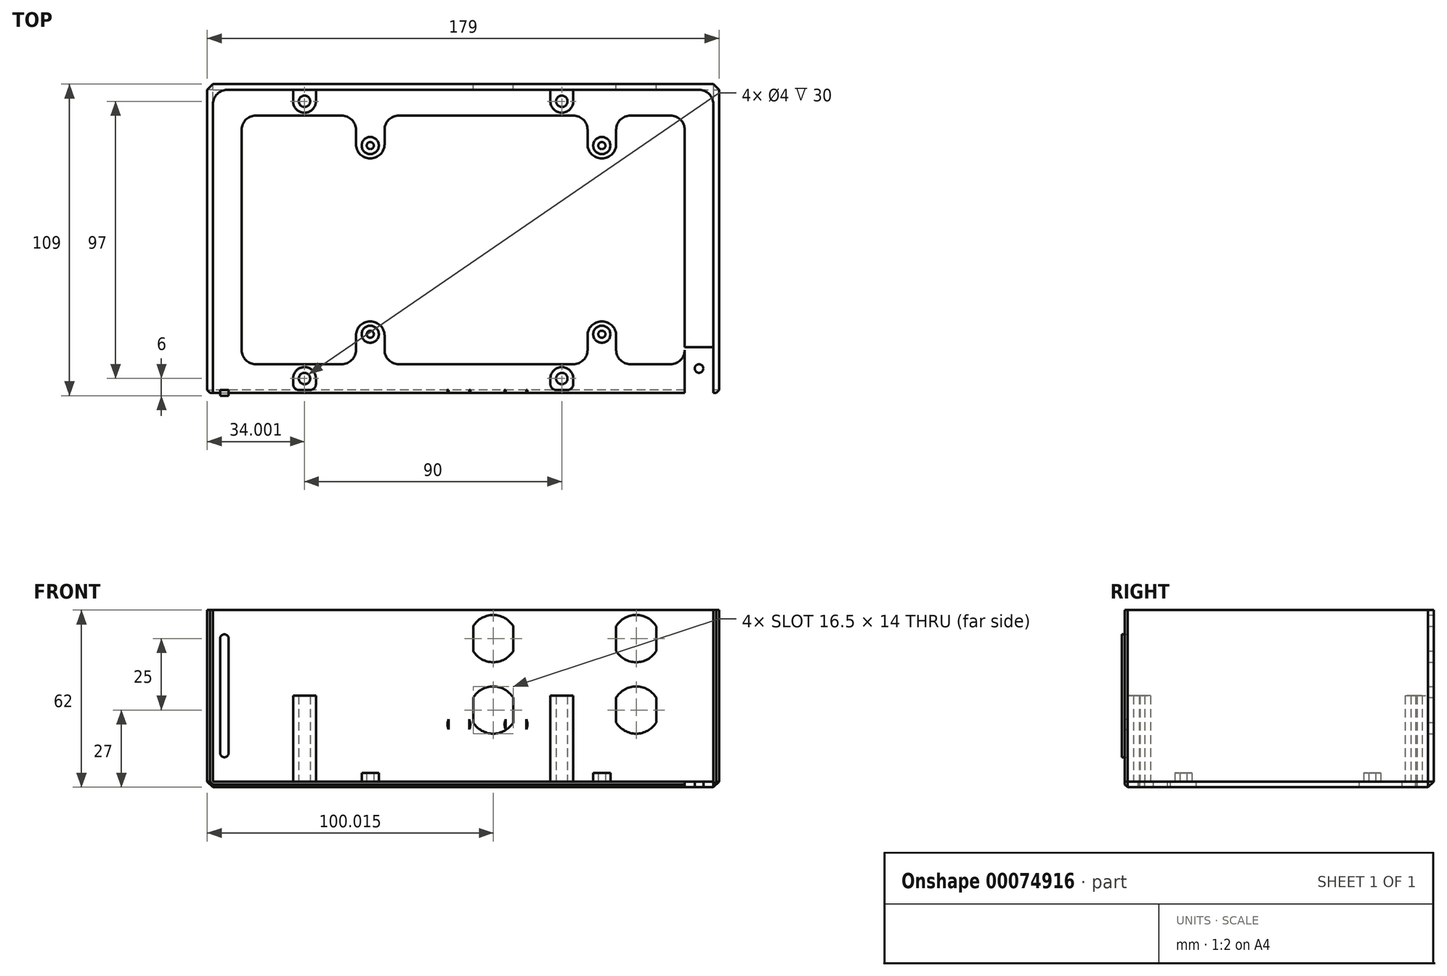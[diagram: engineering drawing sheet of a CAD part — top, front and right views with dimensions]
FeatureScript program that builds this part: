
annotation { "Feature Type Name" : "Feature", "Feature Type Description" : "" }
export const myFeature = defineFeature(function(context is Context, id is Id, definition is map)
    precondition{}
    {
        {
            var Q0;
            Q0=qCreatedBy(makeId("Top.planeOp"),FACE);
            var sketch = newSketch(context, id + "F0", { "sketchPlane" : qUnion([Q0])});
            skLineSegment(sketch, "E0.bottom", {"start": v(-80.27, 52.5) * mm, "end": v(94.73, 52.5) * mm});
            skLineSegment(sketch, "E0.top", {"start": v(-80.27, -52.5) * mm, "end": v(94.73, -52.5) * mm});
            skLineSegment(sketch, "E0.left", {"start": v(-80.27, 52.5) * mm, "end": v(-80.27, -52.5) * mm});
            skLineSegment(sketch, "E0.right", {"start": v(94.73, 52.5) * mm, "end": v(94.73, -52.5) * mm});
            skCircle(sketch, "E1", {"center": v(-25.27, 33) * mm, "radius": 1.25 * mm});
            skCircle(sketch, "E2.0.1.0", {"center": v(-25.27, -33) * mm, "radius": 1.25 * mm});
            skCircle(sketch, "E2.1.0.0", {"center": v(55.73, 33) * mm, "radius": 1.25 * mm});
            skCircle(sketch, "E2.1.1.0", {"center": v(55.73, -33) * mm, "radius": 1.25 * mm});
            skLineSegment(sketch, "E2.direction1", {"start": v(-25.27, 33) * mm, "end": v(55.73, 33) * mm, "construction": true});
            skLineSegment(sketch, "E2.direction2", {"start": v(-25.27, 33) * mm, "end": v(-25.27, -33) * mm, "construction": true});
            skLineSegment(sketch, "E3.bottom", {"start": v(-82.27, 54.5) * mm, "end": v(96.73, 54.5) * mm});
            skLineSegment(sketch, "E3.top", {"start": v(-82.27, -54.5) * mm, "end": v(96.73, -54.5) * mm});
            skLineSegment(sketch, "E3.left", {"start": v(-82.27, 54.5) * mm, "end": v(-82.27, -54.5) * mm});
            skLineSegment(sketch, "E3.right", {"start": v(96.73, 54.5) * mm, "end": v(96.73, -54.5) * mm});
            skCircle(sketch, "E4", {"center": v(-25.27, 33) * mm, "radius": 3 * mm});
            skCircle(sketch, "E5.0.1.0", {"center": v(-25.27, -33) * mm, "radius": 3 * mm});
            skCircle(sketch, "E5.1.0.0", {"center": v(55.73, 33) * mm, "radius": 3 * mm});
            skCircle(sketch, "E5.1.1.0", {"center": v(55.73, -33) * mm, "radius": 3 * mm});
            skLineSegment(sketch, "E6.bottom", {"start": v(-48.27, 42.5) * mm, "end": v(75.73, 42.5) * mm});
            skLineSegment(sketch, "E6.top", {"start": v(-48.27, -42.5) * mm, "end": v(75.73, -42.5) * mm});
            skLineSegment(sketch, "E6.left", {"start": v(-48.27, 42.5) * mm, "end": v(-48.27, -42.5) * mm});
            skLineSegment(sketch, "E6.right", {"start": v(75.73, 42.5) * mm, "end": v(75.73, -42.5) * mm});
            skCircle(sketch, "E7", {"center": v(-48.27, -48.5) * mm, "radius": 2 * mm});
            skCircle(sketch, "E8", {"center": v(-48.27, -48.5) * mm, "radius": 4 * mm});
            skCircle(sketch, "E9.0.1.0", {"center": v(-48.27, 48.5) * mm, "radius": 4 * mm});
            skCircle(sketch, "E9.0.1.1", {"center": v(-48.27, 48.5) * mm, "radius": 2 * mm});
            skCircle(sketch, "E9.1.0.0", {"center": v(41.73, -48.5) * mm, "radius": 4 * mm});
            skCircle(sketch, "E9.1.0.1", {"center": v(41.73, -48.5) * mm, "radius": 2 * mm});
            skCircle(sketch, "E9.1.1.0", {"center": v(41.73, 48.5) * mm, "radius": 4 * mm});
            skCircle(sketch, "E9.1.1.1", {"center": v(41.73, 48.5) * mm, "radius": 2 * mm});
            skLineSegment(sketch, "E9.direction1", {"start": v(-48.27, -48.5) * mm, "end": v(41.73, -48.5) * mm, "construction": true});
            skLineSegment(sketch, "E9.direction2", {"start": v(-48.27, -48.5) * mm, "end": v(-48.27, 48.5) * mm, "construction": true});
            skLineSegment(sketch, "E10", {"start": v(-52.27, -48.55) * mm, "end": v(-52.22, -52.5) * mm});
            skLineSegment(sketch, "E11", {"start": v(-44.27, -48.5) * mm, "end": v(-44.27, -52.5) * mm});
            skLineSegment(sketch, "E12", {"start": v(-52.26, 48.76) * mm, "end": v(-52.26, 52.5) * mm});
            skLineSegment(sketch, "E13", {"start": v(-44.27, 48.54) * mm, "end": v(-44.27, 52.5) * mm});
            skLineSegment(sketch, "E14", {"start": v(37.74, 48.16) * mm, "end": v(37.74, 52.5) * mm});
            skLineSegment(sketch, "E15", {"start": v(45.73, 48.44) * mm, "end": v(45.73, 52.5) * mm});
            skLineSegment(sketch, "E16.MirrorCS", {"start": v(37.74, -48.16) * mm, "end": v(37.74, -52.5) * mm});
            skLineSegment(sketch, "E17.MirrorCS", {"start": v(45.73, -48.44) * mm, "end": v(45.73, -52.5) * mm});
            skLineSegment(sketch, "E18.bottom", {"start": v(94.73, 27.5) * mm, "end": v(84.73, 27.5) * mm});
            skLineSegment(sketch, "E18.top", {"start": v(94.73, 12.5) * mm, "end": v(84.73, 12.5) * mm});
            skLineSegment(sketch, "E18.left", {"start": v(94.73, 27.5) * mm, "end": v(94.73, 12.5) * mm});
            skLineSegment(sketch, "E18.right", {"start": v(84.73, 27.5) * mm, "end": v(84.73, 12.5) * mm});
            skCircle(sketch, "E19", {"center": v(89.73, 20) * mm, "radius": 1.5 * mm});
            skPoint(sketch, "E19.centerSnap0", {"position": v(89.73, 12.5) * mm});
            skPoint(sketch, "E19.centerSnap1", {"position": v(94.73, 20) * mm});
            skLineSegment(sketch, "E20.bottom", {"start": v(94.73, -52.5) * mm, "end": v(84.73, -52.5) * mm});
            skLineSegment(sketch, "E20.top", {"start": v(94.73, -37.5) * mm, "end": v(84.73, -37.5) * mm});
            skLineSegment(sketch, "E20.left", {"start": v(94.73, -52.5) * mm, "end": v(94.73, -37.5) * mm});
            skLineSegment(sketch, "E20.right", {"start": v(84.73, -52.5) * mm, "end": v(84.73, -37.5) * mm});
            skCircle(sketch, "E21", {"center": v(89.73, -45) * mm, "radius": 1.5 * mm});
            skPoint(sketch, "E21.centerSnap0", {"position": v(94.73, -45) * mm});
            skPoint(sketch, "E21.centerSnap1", {"position": v(89.73, -52.5) * mm});
            skSolve(sketch);
        }
        {
            var Q0;
            Q0=qSketchRegion(id+"F0",true);
            var Q1;
            Q1=makeQuery(id+"F0.imprint","IMPRINT",FACE,{"disambiguationData":[TD([[makeQuery(id+"F0.imprint","IMPRINT",EDGE,{"derivedFrom":sQuery(id+"F0.wireOp",EDGE,"E0.bottom")}),-1.0]])]});
            var Q2;
            Q2=makeQuery(id+"F0.imprint","IMPRINT",FACE,{"disambiguationData":[TD([[makeQuery(id+"F0.imprint","IMPRINT",EDGE,{"derivedFrom":sQuery(id+"F0.wireOp",EDGE,"E2.1.1.0")}),-1.0]])]});
            var Q3;
            Q3=makeQuery(id+"F0.imprint","IMPRINT",FACE,{"disambiguationData":[TD([[makeQuery(id+"F0.imprint","IMPRINT",EDGE,{"derivedFrom":sQuery(id+"F0.wireOp",EDGE,"E2.1.1.0")}),1.0]])]});
            var Q4;
            Q4=makeQuery(id+"F0.imprint","IMPRINT",FACE,{"disambiguationData":[TD([[makeQuery(id+"F0.imprint","IMPRINT",EDGE,{"derivedFrom":sQuery(id+"F0.wireOp",EDGE,"E2.0.1.0")}),-1.0]])]});
            var Q5;
            Q5=makeQuery(id+"F0.imprint","IMPRINT",FACE,{"disambiguationData":[TD([[makeQuery(id+"F0.imprint","IMPRINT",EDGE,{"derivedFrom":sQuery(id+"F0.wireOp",EDGE,"E2.0.1.0")}),1.0]])]});
            var Q6;
            Q6=makeQuery(id+"F0.imprint","IMPRINT",FACE,{"disambiguationData":[TD([[makeQuery(id+"F0.imprint","IMPRINT",EDGE,{"derivedFrom":sQuery(id+"F0.wireOp",EDGE,"E1")}),-1.0]])]});
            var Q7;
            Q7=makeQuery(id+"F0.imprint","IMPRINT",FACE,{"disambiguationData":[TD([[makeQuery(id+"F0.imprint","IMPRINT",EDGE,{"derivedFrom":sQuery(id+"F0.wireOp",EDGE,"E1")}),1.0]])]});
            var Q8;
            Q8=makeQuery(id+"F0.imprint","IMPRINT",FACE,{"disambiguationData":[TD([[makeQuery(id+"F0.imprint","IMPRINT",EDGE,{"derivedFrom":sQuery(id+"F0.wireOp",EDGE,"E2.1.0.0")}),-1.0]])]});
            var Q9;
            Q9=makeQuery(id+"F0.imprint","IMPRINT",FACE,{"disambiguationData":[TD([[makeQuery(id+"F0.imprint","IMPRINT",EDGE,{"derivedFrom":sQuery(id+"F0.wireOp",EDGE,"E2.1.0.0")}),1.0]])]});
            var Q10;
            Q10=makeQuery(id+"F0.imprint","IMPRINT",FACE,{"disambiguationData":[TD([[makeQuery(id+"F0.imprint","IMPRINT",EDGE,{"derivedFrom":sQuery(id+"F0.wireOp",EDGE,"E4")}),-1.0]])]});
            var Q11;
            Q11=makeQuery(id+"F0.imprint","IMPRINT",FACE,{"disambiguationData":[TD([[makeQuery(id+"F0.imprint","IMPRINT",EDGE,{"derivedFrom":sQuery(id+"F0.wireOp",EDGE,"E9.1.0.1")}),-1.0]])]});
            var Q12;
            Q12=makeQuery(id+"F0.imprint","IMPRINT",FACE,{"disambiguationData":[TD([[makeQuery(id+"F0.imprint","IMPRINT",EDGE,{"derivedFrom":sQuery(id+"F0.wireOp",EDGE,"E9.1.0.1")}),1.0]])]});
            var Q13;
            {var subQ0=sQuery(id+"F0.wireOp",EDGE,"E16.MirrorCS");var subQ1=sQuery(id+"F0.wireOp",EDGE,"E0.top");var subQ2=makeQuery(id+"F0.imprint","INTERSECT",VERTEX,{"derivedFrom":[subQ1,subQ0]});Q13=makeQuery(id+"F0.imprint","IMPRINT",FACE,{"disambiguationData":[TD([[makeQuery(id+"F0.imprint","IMPRINT",EDGE,{"disambiguationData":[TD([[subQ2,-1.0]])],"derivedFrom":subQ1}),1.0]])]});}
            var Q14;
            Q14=makeQuery(id+"F0.imprint","IMPRINT",FACE,{"disambiguationData":[TD([[makeQuery(id+"F0.imprint","IMPRINT",EDGE,{"derivedFrom":sQuery(id+"F0.wireOp",EDGE,"E7")}),-1.0]])]});
            var Q15;
            Q15=makeQuery(id+"F0.imprint","IMPRINT",FACE,{"disambiguationData":[TD([[makeQuery(id+"F0.imprint","IMPRINT",EDGE,{"derivedFrom":sQuery(id+"F0.wireOp",EDGE,"E7")}),1.0]])]});
            var Q16;
            {var subQ0=sQuery(id+"F0.wireOp",EDGE,"E10");Q16=makeQuery(id+"F0.imprint","IMPRINT",FACE,{"disambiguationData":[TD([[makeQuery(id+"F0.imprint","IMPRINT",EDGE,{"derivedFrom":subQ0}),1.0]])]});}
            var Q17;
            {var subQ0=sQuery(id+"F0.wireOp",EDGE,"E11");Q17=makeQuery(id+"F0.imprint","IMPRINT",FACE,{"disambiguationData":[TD([[makeQuery(id+"F0.imprint","IMPRINT",EDGE,{"derivedFrom":subQ0}),-1.0]])]});}
            var Q18;
            Q18=makeQuery(id+"F0.imprint","IMPRINT",FACE,{"disambiguationData":[TD([[makeQuery(id+"F0.imprint","IMPRINT",EDGE,{"derivedFrom":sQuery(id+"F0.wireOp",EDGE,"E9.0.1.1")}),-1.0]])]});
            var Q19;
            Q19=makeQuery(id+"F0.imprint","IMPRINT",FACE,{"disambiguationData":[TD([[makeQuery(id+"F0.imprint","IMPRINT",EDGE,{"derivedFrom":sQuery(id+"F0.wireOp",EDGE,"E9.0.1.1")}),1.0]])]});
            var Q20;
            {var subQ0=sQuery(id+"F0.wireOp",EDGE,"E13");Q20=makeQuery(id+"F0.imprint","IMPRINT",FACE,{"disambiguationData":[TD([[makeQuery(id+"F0.imprint","IMPRINT",EDGE,{"derivedFrom":subQ0}),1.0]])]});}
            var Q21;
            {var subQ0=sQuery(id+"F0.wireOp",EDGE,"E12");Q21=makeQuery(id+"F0.imprint","IMPRINT",FACE,{"disambiguationData":[TD([[makeQuery(id+"F0.imprint","IMPRINT",EDGE,{"derivedFrom":subQ0}),-1.0]])]});}
            var Q22;
            {var subQ0=sQuery(id+"F0.wireOp",EDGE,"E17.MirrorCS");var subQ1=sQuery(id+"F0.wireOp",EDGE,"E0.top");var subQ2=makeQuery(id+"F0.imprint","INTERSECT",VERTEX,{"derivedFrom":[subQ1,subQ0]});Q22=makeQuery(id+"F0.imprint","IMPRINT",FACE,{"disambiguationData":[TD([[makeQuery(id+"F0.imprint","IMPRINT",EDGE,{"disambiguationData":[TD([[subQ2,1.0]])],"derivedFrom":subQ1}),1.0]])]});}
            var Q23;
            {var subQ0=sQuery(id+"F0.wireOp",EDGE,"E14");var subQ1=sQuery(id+"F0.wireOp",EDGE,"E0.bottom");var subQ2=makeQuery(id+"F0.imprint","INTERSECT",VERTEX,{"derivedFrom":[subQ1,subQ0]});Q23=makeQuery(id+"F0.imprint","IMPRINT",FACE,{"disambiguationData":[TD([[makeQuery(id+"F0.imprint","IMPRINT",EDGE,{"disambiguationData":[TD([[subQ2,-1.0]])],"derivedFrom":subQ1}),-1.0]])]});}
            var Q24;
            {var subQ0=sQuery(id+"F0.wireOp",EDGE,"E15");var subQ1=sQuery(id+"F0.wireOp",EDGE,"E0.bottom");var subQ2=makeQuery(id+"F0.imprint","INTERSECT",VERTEX,{"derivedFrom":[subQ1,subQ0]});Q24=makeQuery(id+"F0.imprint","IMPRINT",FACE,{"disambiguationData":[TD([[makeQuery(id+"F0.imprint","IMPRINT",EDGE,{"disambiguationData":[TD([[subQ2,1.0]])],"derivedFrom":subQ1}),-1.0]])]});}
            var Q25;
            Q25=makeQuery(id+"F0.imprint","IMPRINT",FACE,{"disambiguationData":[TD([[makeQuery(id+"F0.imprint","IMPRINT",EDGE,{"derivedFrom":sQuery(id+"F0.wireOp",EDGE,"E9.1.1.1")}),-1.0]])]});
            var Q26;
            Q26=makeQuery(id+"F0.imprint","IMPRINT",FACE,{"disambiguationData":[TD([[makeQuery(id+"F0.imprint","IMPRINT",EDGE,{"derivedFrom":sQuery(id+"F0.wireOp",EDGE,"E9.1.1.1")}),1.0]])]});
            var Q27;
            Q27=makeQuery(id+"F0.imprint","IMPRINT",FACE,{"disambiguationData":[TD([[makeQuery(id+"F0.imprint","IMPRINT",EDGE,{"derivedFrom":sQuery(id+"F0.wireOp",EDGE,"E18.bottom")}),1.0]])]});
            var Q28;
            Q28=makeQuery(id+"F0.imprint","IMPRINT",FACE,{"disambiguationData":[TD([[makeQuery(id+"F0.imprint","IMPRINT",EDGE,{"derivedFrom":sQuery(id+"F0.wireOp",EDGE,"E20.bottom")}),-1.0]])]});
            var Q29;
            Q29=makeQuery(id+"F0.imprint","IMPRINT",FACE,{"disambiguationData":[TD([[makeQuery(id+"F0.imprint","IMPRINT",EDGE,{"derivedFrom":sQuery(id+"F0.wireOp",EDGE,"E19")}),1.0]])]});
            var Q30;
            Q30=makeQuery(id+"F0.imprint","IMPRINT",FACE,{"disambiguationData":[TD([[makeQuery(id+"F0.imprint","IMPRINT",EDGE,{"derivedFrom":sQuery(id+"F0.wireOp",EDGE,"E21")}),1.0]])]});
            extrude(context, id + "F1", {"entities" : qUnion([Q0, Q1, Q2, Q3, Q4, Q5, Q6, Q7, Q8, Q9, Q10, Q11, Q12, Q13, Q14, Q15, Q16, Q17, Q18, Q19, Q20, Q21, Q22, Q23, Q24, Q25, Q26, Q27, Q28, Q29, Q30]), "oppositeDirection" : true, "depth" : 2 * mm});
        }
        {
            var Q0;
            Q0=makeQuery(id+"F0.imprint","IMPRINT",FACE,{"disambiguationData":[TD([[makeQuery(id+"F0.imprint","IMPRINT",EDGE,{"derivedFrom":sQuery(id+"F0.wireOp",EDGE,"E1")}),-1.0]])]});
            var Q1;
            Q1=makeQuery(id+"F0.imprint","IMPRINT",FACE,{"disambiguationData":[TD([[makeQuery(id+"F0.imprint","IMPRINT",EDGE,{"derivedFrom":sQuery(id+"F0.wireOp",EDGE,"E2.0.1.0")}),-1.0]])]});
            var Q2;
            Q2=makeQuery(id+"F0.imprint","IMPRINT",FACE,{"disambiguationData":[TD([[makeQuery(id+"F0.imprint","IMPRINT",EDGE,{"derivedFrom":sQuery(id+"F0.wireOp",EDGE,"E2.1.0.0")}),-1.0]])]});
            var Q3;
            Q3=makeQuery(id+"F0.imprint","IMPRINT",FACE,{"disambiguationData":[TD([[makeQuery(id+"F0.imprint","IMPRINT",EDGE,{"derivedFrom":sQuery(id+"F0.wireOp",EDGE,"E2.1.1.0")}),-1.0]])]});
            extrude(context, id + "F2", {"entities" : qUnion([Q0, Q1, Q2, Q3]), "operationType" : NewBodyOperationType.ADD, "depth" : 3 * mm});
        }
        {
            var Q0;
            Q0=makeQuery(id+"F0.imprint","IMPRINT",FACE,{"disambiguationData":[TD([[makeQuery(id+"F0.imprint","IMPRINT",EDGE,{"derivedFrom":sQuery(id+"F0.wireOp",EDGE,"E0.bottom")}),1.0]])]});
            extrude(context, id + "F3", {"entities" : qUnion([Q0]), "operationType" : NewBodyOperationType.ADD, "depth" : 60 * mm});
        }
        {
            var Q0;
            Q0=makeQuery(id+"F3.opExtrude","SWEPT_FACE",FACE,{"disambiguationData":[OSD([sQuery(id+"F0.wireOp",EDGE,"E0.top"),sQuery(id+"F0.wireOp",EDGE,"E20.bottom")])]});
            var sketch = newSketch(context, id + "F4", { "sketchPlane" : qUnion([Q0])});
            skCircle(sketch, "E22", {"center": v(-64.73, 20) * mm, "radius": 5.5 * mm});
            skCircle(sketch, "E23", {"center": v(34.27, 20) * mm, "radius": 3.25 * mm});
            skCircle(sketch, "E24.1.0.0", {"center": v(14.27, 20) * mm, "radius": 3.25 * mm});
            skLineSegment(sketch, "E24.direction1", {"start": v(34.27, 20) * mm, "end": v(14.27, 20) * mm, "construction": true});
            skLineSegment(sketch, "E25", {"start": v(76.27, 50) * mm, "end": v(76.27, 10) * mm});
            skArc(sketch, "E26.0.startCap", {"start": v(74.77, 50) * mm, "mid": v(76.27, 51.5) * mm, "end": v(77.77, 50) * mm});
            skArc(sketch, "E26.0.endCap", {"start": v(77.77, 10) * mm, "mid": v(76.27, 8.5) * mm, "end": v(74.77, 10) * mm});
            skLineSegment(sketch, "E26.0.left", {"start": v(77.77, 50) * mm, "end": v(77.77, 10) * mm});
            skLineSegment(sketch, "E26.0.right", {"start": v(74.77, 50) * mm, "end": v(74.77, 10) * mm});
            skCircle(sketch, "E27", {"center": v(-5.73, 20) * mm, "radius": 4 * mm});
            skCircle(sketch, "E28.1.0.2", {"center": v(-25.73, 20) * mm, "radius": 4 * mm});
            skLineSegment(sketch, "E28.direction1", {"start": v(-9.62, 20.95) * mm, "end": v(-29.62, 20.95) * mm, "construction": true});
            skLineSegment(sketch, "E29", {"start": v(-29.33, 23.3) * mm, "end": v(-29.33, 15.56) * mm, "construction": true});
            skLineSegment(sketch, "E30", {"start": v(-29.33, 15.56) * mm, "end": v(-22.13, 15.56) * mm, "construction": true});
            skLineSegment(sketch, "E31", {"start": v(-22.13, 15.56) * mm, "end": v(-22.13, 24.42) * mm, "construction": true});
            skLineSegment(sketch, "E32", {"start": v(-22.13, 21.74) * mm, "end": v(-22.13, 18.26) * mm});
            skLineSegment(sketch, "E33", {"start": v(-29.33, 21.74) * mm, "end": v(-29.33, 18.26) * mm});
            skLineSegment(sketch, "E34.1.0.0", {"start": v(-9.33, 21.74) * mm, "end": v(-9.33, 18.26) * mm});
            skLineSegment(sketch, "E34.1.0.1", {"start": v(-2.13, 21.74) * mm, "end": v(-2.13, 18.26) * mm});
            skLineSegment(sketch, "E34.direction1", {"start": v(-29.33, 18.26) * mm, "end": v(-9.33, 18.26) * mm, "construction": true});
            skSolve(sketch);
        }
        {
            var Q0;
            Q0=makeQuery(id+"F4.imprint","IMPRINT",FACE,{"disambiguationData":[TD([[makeQuery(id+"F4.imprint","IMPRINT",EDGE,{"derivedFrom":sQuery(id+"F4.wireOp",EDGE,"E22")}),1.0]])]});
            var Q1;
            {var subQ0=sQuery(id+"F4.wireOp",EDGE,"E32");Q1=makeQuery(id+"F4.imprint","IMPRINT",FACE,{"disambiguationData":[TD([[makeQuery(id+"F4.imprint","IMPRINT",EDGE,{"derivedFrom":subQ0}),-1.0]])]});}
            var Q2;
            {var subQ0=sQuery(id+"F4.wireOp",EDGE,"E34.1.0.0");Q2=makeQuery(id+"F4.imprint","IMPRINT",FACE,{"disambiguationData":[TD([[makeQuery(id+"F4.imprint","IMPRINT",EDGE,{"derivedFrom":subQ0}),1.0]])]});}
            var Q3;
            Q3=makeQuery(id+"F4.imprint","IMPRINT",FACE,{"disambiguationData":[TD([[makeQuery(id+"F4.imprint","IMPRINT",EDGE,{"derivedFrom":sQuery(id+"F4.wireOp",EDGE,"E24.1.0.0")}),1.0]])]});
            var Q4;
            Q4=makeQuery(id+"F4.imprint","IMPRINT",FACE,{"disambiguationData":[TD([[makeQuery(id+"F4.imprint","IMPRINT",EDGE,{"derivedFrom":sQuery(id+"F4.wireOp",EDGE,"E23")}),1.0]])]});
            var Q5;
            Q5=makeQuery(id+"F4.imprint","IMPRINT",FACE,{"disambiguationData":[TD([[makeQuery(id+"F4.imprint","IMPRINT",EDGE,{"derivedFrom":sQuery(id+"F4.wireOp",EDGE,"E26.0.startCap")}),-1.0]])]});
            extrude(context, id + "F5", {"entities" : qUnion([Q0, Q1, Q2, Q3, Q4, Q5]), "operationType" : NewBodyOperationType.REMOVE, "endBound" : BoundingType.UP_TO_NEXT, "oppositeDirection" : true, "depth" : 25 * mm});
        }
        {
            var Q0;
            Q0=makeQuery(id+"F0.imprint","IMPRINT",FACE,{"disambiguationData":[TD([[makeQuery(id+"F0.imprint","IMPRINT",EDGE,{"derivedFrom":sQuery(id+"F0.wireOp",EDGE,"E9.0.1.1")}),-1.0]])]});
            var Q1;
            {var subQ0=sQuery(id+"F0.wireOp",EDGE,"E12");Q1=makeQuery(id+"F0.imprint","IMPRINT",FACE,{"disambiguationData":[TD([[makeQuery(id+"F0.imprint","IMPRINT",EDGE,{"derivedFrom":subQ0}),-1.0]])]});}
            var Q2;
            {var subQ0=sQuery(id+"F0.wireOp",EDGE,"E13");Q2=makeQuery(id+"F0.imprint","IMPRINT",FACE,{"disambiguationData":[TD([[makeQuery(id+"F0.imprint","IMPRINT",EDGE,{"derivedFrom":subQ0}),1.0]])]});}
            var Q3;
            {var subQ0=sQuery(id+"F0.wireOp",EDGE,"E14");var subQ1=sQuery(id+"F0.wireOp",EDGE,"E0.bottom");var subQ2=makeQuery(id+"F0.imprint","INTERSECT",VERTEX,{"derivedFrom":[subQ1,subQ0]});Q3=makeQuery(id+"F0.imprint","IMPRINT",FACE,{"disambiguationData":[TD([[makeQuery(id+"F0.imprint","IMPRINT",EDGE,{"disambiguationData":[TD([[subQ2,-1.0]])],"derivedFrom":subQ1}),-1.0]])]});}
            var Q4;
            {var subQ0=sQuery(id+"F0.wireOp",EDGE,"E15");var subQ1=sQuery(id+"F0.wireOp",EDGE,"E0.bottom");var subQ2=makeQuery(id+"F0.imprint","INTERSECT",VERTEX,{"derivedFrom":[subQ1,subQ0]});Q4=makeQuery(id+"F0.imprint","IMPRINT",FACE,{"disambiguationData":[TD([[makeQuery(id+"F0.imprint","IMPRINT",EDGE,{"disambiguationData":[TD([[subQ2,1.0]])],"derivedFrom":subQ1}),-1.0]])]});}
            var Q5;
            Q5=makeQuery(id+"F0.imprint","IMPRINT",FACE,{"disambiguationData":[TD([[makeQuery(id+"F0.imprint","IMPRINT",EDGE,{"derivedFrom":sQuery(id+"F0.wireOp",EDGE,"E9.1.1.1")}),-1.0]])]});
            var Q6;
            Q6=makeQuery(id+"F0.imprint","IMPRINT",FACE,{"disambiguationData":[TD([[makeQuery(id+"F0.imprint","IMPRINT",EDGE,{"derivedFrom":sQuery(id+"F0.wireOp",EDGE,"E7")}),-1.0]])]});
            var Q7;
            {var subQ0=sQuery(id+"F0.wireOp",EDGE,"E10");Q7=makeQuery(id+"F0.imprint","IMPRINT",FACE,{"disambiguationData":[TD([[makeQuery(id+"F0.imprint","IMPRINT",EDGE,{"derivedFrom":subQ0}),1.0]])]});}
            var Q8;
            {var subQ0=sQuery(id+"F0.wireOp",EDGE,"E11");Q8=makeQuery(id+"F0.imprint","IMPRINT",FACE,{"disambiguationData":[TD([[makeQuery(id+"F0.imprint","IMPRINT",EDGE,{"derivedFrom":subQ0}),-1.0]])]});}
            var Q9;
            {var subQ0=sQuery(id+"F0.wireOp",EDGE,"E16.MirrorCS");var subQ1=sQuery(id+"F0.wireOp",EDGE,"E0.top");var subQ2=makeQuery(id+"F0.imprint","INTERSECT",VERTEX,{"derivedFrom":[subQ1,subQ0]});Q9=makeQuery(id+"F0.imprint","IMPRINT",FACE,{"disambiguationData":[TD([[makeQuery(id+"F0.imprint","IMPRINT",EDGE,{"disambiguationData":[TD([[subQ2,-1.0]])],"derivedFrom":subQ1}),1.0]])]});}
            var Q10;
            Q10=makeQuery(id+"F0.imprint","IMPRINT",FACE,{"disambiguationData":[TD([[makeQuery(id+"F0.imprint","IMPRINT",EDGE,{"derivedFrom":sQuery(id+"F0.wireOp",EDGE,"E9.1.0.1")}),-1.0]])]});
            var Q11;
            {var subQ0=sQuery(id+"F0.wireOp",EDGE,"E17.MirrorCS");var subQ1=sQuery(id+"F0.wireOp",EDGE,"E0.top");var subQ2=makeQuery(id+"F0.imprint","INTERSECT",VERTEX,{"derivedFrom":[subQ1,subQ0]});Q11=makeQuery(id+"F0.imprint","IMPRINT",FACE,{"disambiguationData":[TD([[makeQuery(id+"F0.imprint","IMPRINT",EDGE,{"disambiguationData":[TD([[subQ2,1.0]])],"derivedFrom":subQ1}),1.0]])]});}
            extrude(context, id + "F6", {"entities" : qUnion([Q0, Q1, Q2, Q3, Q4, Q5, Q6, Q7, Q8, Q9, Q10, Q11]), "operationType" : NewBodyOperationType.ADD, "depth" : 30 * mm});
        }
        {
            var Q0;
            Q0=makeQuery(id+"F6.opExtrude","SWEPT_EDGE",EDGE,{"disambiguationData":[OSD([sQuery(id+"F0.wireOp",EDGE,"E0.top"),sQuery(id+"F0.wireOp",EDGE,"E10")])]});
            var Q1;
            Q1=makeQuery(id+"F6.opExtrude","SWEPT_EDGE",EDGE,{"disambiguationData":[OSD([sQuery(id+"F0.wireOp",EDGE,"E0.top"),sQuery(id+"F0.wireOp",EDGE,"E11")])]});
            var Q2;
            Q2=makeQuery(id+"F6.opExtrude","SWEPT_EDGE",EDGE,{"disambiguationData":[OSD([sQuery(id+"F0.wireOp",EDGE,"E0.top"),sQuery(id+"F0.wireOp",EDGE,"E16.MirrorCS")])]});
            var Q3;
            Q3=makeQuery(id+"F6.opExtrude","SWEPT_EDGE",EDGE,{"disambiguationData":[OSD([sQuery(id+"F0.wireOp",EDGE,"E0.top"),sQuery(id+"F0.wireOp",EDGE,"E17.MirrorCS")])]});
            var Q4;
            Q4=makeQuery(id+"F6.opExtrude","SWEPT_EDGE",EDGE,{"disambiguationData":[OSD([sQuery(id+"F0.wireOp",EDGE,"E0.bottom"),sQuery(id+"F0.wireOp",EDGE,"E15")])]});
            var Q5;
            Q5=makeQuery(id+"F6.opExtrude","SWEPT_EDGE",EDGE,{"disambiguationData":[OSD([sQuery(id+"F0.wireOp",EDGE,"E0.bottom"),sQuery(id+"F0.wireOp",EDGE,"E14")])]});
            var Q6;
            Q6=makeQuery(id+"F6.opExtrude","SWEPT_EDGE",EDGE,{"disambiguationData":[OSD([sQuery(id+"F0.wireOp",EDGE,"E0.bottom"),sQuery(id+"F0.wireOp",EDGE,"E13")])]});
            var Q7;
            Q7=makeQuery(id+"F6.opExtrude","SWEPT_EDGE",EDGE,{"disambiguationData":[OSD([sQuery(id+"F0.wireOp",EDGE,"E0.bottom"),sQuery(id+"F0.wireOp",EDGE,"E12")])]});
            fillet(context, id + "F7", {"entities" : qUnion([Q0, Q1, Q2, Q3, Q4, Q5, Q6, Q7]), "radius" : 2 * mm, "tangentPropagation" : true, "allowEdgeOverflow" : false});
        }
        {
            var Q0;
            Q0=makeQuery(id+"F3.opExtrude","SWEPT_EDGE",EDGE,{"disambiguationData":[OSD([sQuery(id+"F0.wireOp",EDGE,"E0.top"),sQuery(id+"F0.wireOp",EDGE,"E0.right")])]});
            var Q1;
            Q1=makeQuery(id+"F3.opExtrude","SWEPT_EDGE",EDGE,{"disambiguationData":[OSD([sQuery(id+"F0.wireOp",EDGE,"E0.top"),sQuery(id+"F0.wireOp",EDGE,"E0.left")])]});
            var Q2;
            Q2=makeQuery(id+"F3.opExtrude","SWEPT_EDGE",EDGE,{"disambiguationData":[OSD([sQuery(id+"F0.wireOp",EDGE,"E0.bottom"),sQuery(id+"F0.wireOp",EDGE,"E0.right")])]});
            var Q3;
            Q3=makeQuery(id+"F3.opExtrude","SWEPT_EDGE",EDGE,{"disambiguationData":[OSD([sQuery(id+"F0.wireOp",EDGE,"E0.bottom"),sQuery(id+"F0.wireOp",EDGE,"E0.left")])]});
            var Q4;
            Q4=makeQuery(id+"FWUeCJMCAEF3pSk_1.opExtrude","SWEPT_EDGE",EDGE,{"disambiguationData":[OSD([sQuery(id+"F0.wireOp",EDGE,"E0.top"),sQuery(id+"F0.wireOp",EDGE,"E20.bottom"),sQuery(id+"F0.wireOp",EDGE,"E20.right")])]});
            var Q5;
            Q5=makeQuery(id+"FWUeCJMCAEF3pSk_1.opExtrude","SWEPT_EDGE",EDGE,{"disambiguationData":[OSD([sQuery(id+"F0.wireOp",EDGE,"E0.right"),sQuery(id+"F0.wireOp",EDGE,"E20.top"),sQuery(id+"F0.wireOp",EDGE,"E20.left")])]});
            var Q6;
            Q6=makeQuery(id+"FWUeCJMCAEF3pSk_1.opExtrude","SWEPT_EDGE",EDGE,{"disambiguationData":[OSD([sQuery(id+"F0.wireOp",EDGE,"E0.right"),sQuery(id+"F0.wireOp",EDGE,"E18.top"),sQuery(id+"F0.wireOp",EDGE,"E18.left")])]});
            var Q7;
            Q7=makeQuery(id+"FWUeCJMCAEF3pSk_1.opExtrude","SWEPT_EDGE",EDGE,{"disambiguationData":[OSD([sQuery(id+"F0.wireOp",EDGE,"E0.right"),sQuery(id+"F0.wireOp",EDGE,"E18.bottom"),sQuery(id+"F0.wireOp",EDGE,"E18.left")])]});
            var Q8;
            Q8=makeQuery(id+"F3.opExtrude","SWEPT_EDGE",EDGE,{"disambiguationData":[OSD([sQuery(id+"F0.wireOp",EDGE,"E20.bottom"),sQuery(id+"F0.wireOp",EDGE,"E20.left")])]});
            fillet(context, id + "F8", {"entities" : qUnion([Q0, Q1, Q2, Q3, Q4, Q5, Q6, Q7, Q8]), "radius" : 5 * mm, "tangentPropagation" : true, "allowEdgeOverflow" : false});
        }
        {
            var Q0;
            {var subQ0=sQuery(id+"F0.wireOp",EDGE,"E3.left");var subQ1=sQuery(id+"F0.wireOp",EDGE,"E3.top");Q0=makeQuery(id+"F3.boolean.opBoolean","MERGE",EDGE,{"derivedFrom":[makeQuery(id+"F1.opExtrude","SWEPT_EDGE",EDGE,{"disambiguationData":[OSD([subQ1,subQ0])]}),makeQuery(id+"F3.opExtrude","SWEPT_EDGE",EDGE,{"disambiguationData":[OSD([subQ1,subQ0])]})]});}
            var Q1;
            {var subQ0=sQuery(id+"F0.wireOp",EDGE,"E3.left");var subQ1=sQuery(id+"F0.wireOp",EDGE,"E3.bottom");Q1=makeQuery(id+"F3.boolean.opBoolean","MERGE",EDGE,{"derivedFrom":[makeQuery(id+"F1.opExtrude","SWEPT_EDGE",EDGE,{"disambiguationData":[OSD([subQ1,subQ0])]}),makeQuery(id+"F3.opExtrude","SWEPT_EDGE",EDGE,{"disambiguationData":[OSD([subQ1,subQ0])]})]});}
            var Q2;
            {var subQ0=sQuery(id+"F0.wireOp",EDGE,"E3.right");var subQ1=sQuery(id+"F0.wireOp",EDGE,"E3.bottom");Q2=makeQuery(id+"F3.boolean.opBoolean","MERGE",EDGE,{"derivedFrom":[makeQuery(id+"F1.opExtrude","SWEPT_EDGE",EDGE,{"disambiguationData":[OSD([subQ1,subQ0])]}),makeQuery(id+"F3.opExtrude","SWEPT_EDGE",EDGE,{"disambiguationData":[OSD([subQ1,subQ0])]})]});}
            var Q3;
            {var subQ0=sQuery(id+"F0.wireOp",EDGE,"E3.right");var subQ1=sQuery(id+"F0.wireOp",EDGE,"E3.top");Q3=makeQuery(id+"F3.boolean.opBoolean","MERGE",EDGE,{"derivedFrom":[makeQuery(id+"F1.opExtrude","SWEPT_EDGE",EDGE,{"disambiguationData":[OSD([subQ1,subQ0])]}),makeQuery(id+"F3.opExtrude","SWEPT_EDGE",EDGE,{"disambiguationData":[OSD([subQ1,subQ0])]})]});}
            var Q4;
            Q4=makeQuery(id+"F1.opExtrude","CAP_EDGE",EDGE,{"disambiguationData":[OSD([sQuery(id+"F0.wireOp",EDGE,"E3.right")])],"isStart":false});
            var Q5;
            Q5=makeQuery(id+"F1.opExtrude","CAP_EDGE",EDGE,{"disambiguationData":[OSD([sQuery(id+"F0.wireOp",EDGE,"E3.left")])],"isStart":false});
            var Q6;
            Q6=makeQuery(id+"F1.opExtrude","CAP_EDGE",EDGE,{"disambiguationData":[OSD([sQuery(id+"F0.wireOp",EDGE,"E3.top")])],"isStart":false});
            var Q7;
            Q7=makeQuery(id+"F1.opExtrude","CAP_EDGE",EDGE,{"disambiguationData":[OSD([sQuery(id+"F0.wireOp",EDGE,"E3.bottom")])],"isStart":false});
            chamfer(context, id + "F9", {"entities" : qUnion([Q0, Q1, Q2, Q3, Q4, Q5, Q6, Q7]), "width" : 2 * mm, "tangentPropagation" : true});
        }
        {
            var Q0;
            {var subQ0=sQuery(id+"F0.wireOp",EDGE,"E3.top");Q0=makeQuery(id+"F3.boolean.opBoolean","MERGE",FACE,{"derivedFrom":[makeQuery(id+"F1.opExtrude","SWEPT_FACE",FACE,{"disambiguationData":[OSD([subQ0])]}),makeQuery(id+"F3.opExtrude","SWEPT_FACE",FACE,{"disambiguationData":[OSD([subQ0])]})]});}
            var sketch = newSketch(context, id + "F10", { "sketchPlane" : qUnion([Q0])});
            skArc(sketch, "E35", {"start": v(-37.74, 34.14) * mm, "mid": v(-34.27, 35.58) * mm, "end": v(-30.8, 34.14) * mm, "construction": true});
            skLineSegment(sketch, "E36", {"start": v(-34.27, 30.68) * mm, "end": v(-37.74, 34.14) * mm, "construction": true});
            skLineSegment(sketch, "E37", {"start": v(-34.27, 30.68) * mm, "end": v(-34.27, 42.11) * mm, "construction": true});
            skLineSegment(sketch, "E38", {"start": v(-34.27, 30.68) * mm, "end": v(-30.8, 34.14) * mm, "construction": true});
            skArc(sketch, "E39.0", {"start": v(-41.27, 37.68) * mm, "mid": v(-34.27, 40.58) * mm, "end": v(-27.26, 37.68) * mm, "construction": true});
            skLineSegment(sketch, "E40.0", {"start": v(-84.27, -8) * mm, "end": v(98.73, -8) * mm});
            skLineSegment(sketch, "E40.1", {"start": v(-84.27, 75) * mm, "end": v(-84.27, -8) * mm});
            skLineSegment(sketch, "E40.2", {"start": v(98.73, 75) * mm, "end": v(-84.27, 75) * mm});
            skLineSegment(sketch, "E40.3", {"start": v(98.73, -8) * mm, "end": v(98.73, 75) * mm});
            skArc(sketch, "E41.0", {"start": v(-44.8, 41.22) * mm, "mid": v(-34.27, 45.58) * mm, "end": v(-23.73, 41.22) * mm, "construction": true});
            skArc(sketch, "E42.0.startCap", {"start": v(-44.1, 40.5) * mm, "mid": v(-45.52, 40.5) * mm, "end": v(-45.52, 41.92) * mm});
            skArc(sketch, "E42.0.endCap", {"start": v(-23.02, 41.92) * mm, "mid": v(-23.02, 40.5) * mm, "end": v(-24.44, 40.5) * mm});
            skArc(sketch, "E42.0.left", {"start": v(-45.52, 41.92) * mm, "mid": v(-34.27, 46.58) * mm, "end": v(-23.02, 41.92) * mm});
            skArc(sketch, "E42.0.right", {"start": v(-44.1, 40.5) * mm, "mid": v(-34.27, 44.58) * mm, "end": v(-24.44, 40.5) * mm});
            skArc(sketch, "E43.0.startCap", {"start": v(-40.57, 36.97) * mm, "mid": v(-41.98, 36.97) * mm, "end": v(-41.98, 38.39) * mm});
            skArc(sketch, "E43.0.endCap", {"start": v(-26.56, 38.39) * mm, "mid": v(-26.56, 36.97) * mm, "end": v(-27.97, 36.97) * mm});
            skArc(sketch, "E43.0.left", {"start": v(-41.98, 38.39) * mm, "mid": v(-34.27, 41.58) * mm, "end": v(-26.56, 38.39) * mm});
            skArc(sketch, "E43.0.right", {"start": v(-40.57, 36.97) * mm, "mid": v(-34.27, 39.58) * mm, "end": v(-27.97, 36.97) * mm});
            skArc(sketch, "E43.1.startCap", {"start": v(-37.03, 33.44) * mm, "mid": v(-38.45, 33.44) * mm, "end": v(-38.45, 34.85) * mm});
            skArc(sketch, "E43.1.endCap", {"start": v(-30.1, 34.85) * mm, "mid": v(-30.1, 33.44) * mm, "end": v(-31.5, 33.44) * mm});
            skArc(sketch, "E43.1.left", {"start": v(-38.45, 34.85) * mm, "mid": v(-34.27, 36.58) * mm, "end": v(-30.1, 34.85) * mm});
            skArc(sketch, "E43.1.right", {"start": v(-37.03, 33.44) * mm, "mid": v(-34.27, 34.58) * mm, "end": v(-31.5, 33.44) * mm});
            skLineSegment(sketch, "E44", {"start": v(-14.27, 20) * mm, "end": v(-14.27, 54.13) * mm, "construction": true});
            skLineSegment(sketch, "E45", {"start": v(-14.27, 30.68) * mm, "end": v(-14.27, 54.13) * mm, "construction": true});
            skLineSegment(sketch, "E46", {"start": v(-14.27, 46.58) * mm, "end": v(-21, 54.13) * mm, "construction": true});
            skPoint(sketch, "E46.startSnap0", {"position": v(-34.27, 46.58) * mm});
            skLineSegment(sketch, "E47.MirrorCS", {"start": v(-14.27, 46.58) * mm, "end": v(-7.53, 54.13) * mm, "construction": true});
            skArc(sketch, "E48.0.endCap", {"start": v(-21.75, 53.47) * mm, "mid": v(-21.67, 54.88) * mm, "end": v(-20.26, 54.8) * mm});
            skLineSegment(sketch, "E48.0.left", {"start": v(-15.27, 46.2) * mm, "end": v(-21.75, 53.47) * mm});
            skArc(sketch, "E48.1.startCap", {"start": v(-13.27, 30.68) * mm, "mid": v(-14.27, 29.68) * mm, "end": v(-15.27, 30.68) * mm});
            skArc(sketch, "E48.1.endCap", {"start": v(-15.27, 54.13) * mm, "mid": v(-14.27, 55.13) * mm, "end": v(-13.27, 54.13) * mm});
            skLineSegment(sketch, "E48.1.left", {"start": v(-15.27, 30.68) * mm, "end": v(-15.27, 46.2) * mm});
            skLineSegment(sketch, "E48.1.right", {"start": v(-13.27, 30.68) * mm, "end": v(-13.27, 46.2) * mm});
            skArc(sketch, "E48.2.endCap", {"start": v(-8.28, 54.8) * mm, "mid": v(-6.86, 54.88) * mm, "end": v(-6.78, 53.47) * mm});
            skLineSegment(sketch, "E48.2.right", {"start": v(-13.27, 46.2) * mm, "end": v(-6.78, 53.47) * mm});
            skFitSpline(sketch, "E49", {"points": [v(4.97, 32.4) * mm, v(9.8, 35.55) * mm, v(10.9, 40.93) * mm, v(12.76, 47.98) * mm, v(15.73, 49.65) * mm], "startDerivative": vector(22.47, 10.26) * mm, "endDerivative": vector(16.5, 4.85) * mm});
            skLineSegment(sketch, "E50", {"start": v(6.9, 33.32) * mm, "end": v(6.9, 31.48) * mm});
            skLineSegment(sketch, "E51", {"start": v(6.9, 31.48) * mm, "end": v(15.73, 31.48) * mm});
            skLineSegment(sketch, "E52", {"start": v(15.73, 49.65) * mm, "end": v(15.73, 31.48) * mm, "construction": true});
            skFitSpline(sketch, "E53.MirrorCS", {"points": [v(26.5, 32.4) * mm, v(21.67, 35.55) * mm, v(20.55, 40.93) * mm, v(18.7, 47.98) * mm, v(15.73, 49.65) * mm], "startDerivative": vector(-22.47, 10.26) * mm, "endDerivative": vector(-16.5, 4.85) * mm});
            skLineSegment(sketch, "E54.MirrorCS", {"start": v(24.55, 33.32) * mm, "end": v(24.55, 31.48) * mm});
            skLineSegment(sketch, "E55.MirrorCS", {"start": v(24.55, 31.48) * mm, "end": v(15.73, 31.48) * mm});
            skArc(sketch, "E56", {"start": v(16.96, 31.48) * mm, "mid": v(15.73, 30.25) * mm, "end": v(14.5, 31.48) * mm});
            skPoint(sketch, "E57.orphan", {"position": v(15.73, 30.25) * mm});
            skPoint(sketch, "E58.orphan", {"position": v(70.94, 44.45) * mm});
            skPoint(sketch, "E59.1.4", {"position": v(71.6, 50.06) * mm});
            skLineSegment(sketch, "E59.2.0", {"start": v(65.73, 40.4) * mm, "end": v(55.73, 46.17) * mm});
            skLineSegment(sketch, "E59.2.1", {"start": v(59.73, 30) * mm, "end": v(74.4, 42.31) * mm});
            skLineSegment(sketch, "E59.2.2", {"start": v(64.4, 48.09) * mm, "end": v(74.4, 42.31) * mm});
            skLineSegment(sketch, "E59.2.3", {"start": v(70.4, 58.48) * mm, "end": v(55.73, 46.17) * mm});
            skPoint(sketch, "E59.2.4", {"position": v(66.41, 47.83) * mm});
            skLineSegment(sketch, "E60", {"start": v(65.73, 40.4) * mm, "end": v(59.73, 30) * mm});
            skLineSegment(sketch, "E61", {"start": v(64.4, 48.09) * mm, "end": v(70.4, 58.48) * mm});
            skText(sketch, "E62", { "text": "1", "fontName": "DroidSansMono.ttf"});
            skText(sketch, "E63", { "text": "2", "fontName": "DroidSansMono.ttf"});
            skLineSegment(sketch, "E64.trimOffspring", {"start": v(-15.27, 49.2) * mm, "end": v(-15.27, 54.13) * mm});
            skLineSegment(sketch, "E65.trimOffspring", {"start": v(-15.27, 49.2) * mm, "end": v(-20.26, 54.8) * mm});
            skLineSegment(sketch, "E66.trimOffspring", {"start": v(-13.27, 49.2) * mm, "end": v(-13.27, 54.13) * mm});
            skLineSegment(sketch, "E67.trimOffspring", {"start": v(-13.27, 49.2) * mm, "end": v(-8.28, 54.8) * mm});
            const initialGuessF10  = {"E62": [0.00217, 0.00538, 1, 0, 0.00778], "E63": [0.0221, 0.00538, 1, 0, 0.00778]};
            skSetInitialGuess(sketch, initialGuessF10);
            skSolve(sketch);
        }
        {
            var Q0;
            Q0=makeQuery(id+"F10.imprint","IMPRINT",FACE,{"disambiguationData":[TD([[makeQuery(id+"F10.imprint","IMPRINT",EDGE,{"derivedFrom":sQuery(id+"F10.wireOp",EDGE,"E42.0.startCap")}),-1.0]])]});
            var Q1;
            Q1=makeQuery(id+"F10.imprint","IMPRINT",FACE,{"disambiguationData":[TD([[makeQuery(id+"F10.imprint","IMPRINT",EDGE,{"derivedFrom":sQuery(id+"F10.wireOp",EDGE,"E43.0.startCap")}),-1.0]])]});
            var Q2;
            Q2=makeQuery(id+"F10.imprint","IMPRINT",FACE,{"disambiguationData":[TD([[makeQuery(id+"F10.imprint","IMPRINT",EDGE,{"derivedFrom":sQuery(id+"F10.wireOp",EDGE,"E43.1.startCap")}),-1.0]])]});
            var Q3;
            Q3=makeQuery(id+"F10.imprint","IMPRINT",FACE,{"disambiguationData":[TD([[makeQuery(id+"F10.imprint","IMPRINT",EDGE,{"derivedFrom":sQuery(id+"F10.wireOp",EDGE,"E49")}),-1.0]])]});
            var Q4;
            {var subQ3=sQuery(id+"F10.wireOp",EDGE,"E56");Q4=makeQuery(id+"F10.imprint","IMPRINT",FACE,{"disambiguationData":[TD([[makeQuery(id+"F10.imprint","IMPRINT",EDGE,{"derivedFrom":subQ3}),-1.0]])]});}
            var Q5;
            Q5=makeQuery(id+"F10.imprint","IMPRINT",FACE,{"disambiguationData":[TD([[makeQuery(id+"F10.imprint","IMPRINT",EDGE,{"derivedFrom":sQuery(id+"F10.wireOp",EDGE,"E62.sketch_text.stroke-0")}),-1.0]])]});
            var Q6;
            Q6=makeQuery(id+"F10.imprint","IMPRINT",FACE,{"disambiguationData":[TD([[makeQuery(id+"F10.imprint","IMPRINT",EDGE,{"derivedFrom":sQuery(id+"F10.wireOp",EDGE,"E63.sketch_text.stroke-0")}),-1.0]])]});
            var Q7;
            Q7=makeQuery(id+"F10.imprint","IMPRINT",FACE,{"disambiguationData":[TD([[makeQuery(id+"F10.imprint","IMPRINT",EDGE,{"derivedFrom":sQuery(id+"F10.wireOp",EDGE,"E59.2.0")}),-1.0]])]});
            var Q8;
            Q8=makeQuery(id+"F10.imprint","IMPRINT",FACE,{"disambiguationData":[TD([[makeQuery(id+"F10.imprint","IMPRINT",EDGE,{"derivedFrom":sQuery(id+"F10.wireOp",EDGE,"E48.0.endCap")}),-1.0]])]});
            extrude(context, id + "F11", {"entities" : qUnion([Q0, Q1, Q2, Q3, Q4, Q5, Q6, Q7, Q8]), "operationType" : NewBodyOperationType.REMOVE, "oppositeDirection" : true, "depth" : 1 * mm});
        }
        {
            var Q0;
            {var subQ0=sQuery(id+"F0.wireOp",EDGE,"E3.bottom");Q0=makeQuery(id+"F3.boolean.opBoolean","MERGE",FACE,{"derivedFrom":[makeQuery(id+"F1.opExtrude","SWEPT_FACE",FACE,{"disambiguationData":[OSD([subQ0])]}),makeQuery(id+"F3.opExtrude","SWEPT_FACE",FACE,{"disambiguationData":[OSD([subQ0])]})]});}
            var sketch = newSketch(context, id + "F12", { "sketchPlane" : qUnion([Q0])});
            skCircle(sketch, "E68", {"center": v(-67.74, 25) * mm, "radius": 8.25 * mm});
            skLineSegment(sketch, "E69", {"start": v(-74.74, 30.49) * mm, "end": v(-74.74, 3.5) * mm, "construction": true});
            skLineSegment(sketch, "E70", {"start": v(-60.74, 36.2) * mm, "end": v(-60.74, 10.6) * mm, "construction": true});
            skLineSegment(sketch, "E71", {"start": v(-60.74, 29.37) * mm, "end": v(-60.74, 20.63) * mm});
            skLineSegment(sketch, "E72", {"start": v(-74.74, 20.63) * mm, "end": v(-74.74, 29.37) * mm});
            skCircle(sketch, "E73.1.0.0", {"center": v(-17.74, 25) * mm, "radius": 8.25 * mm});
            skLineSegment(sketch, "E73.1.0.1", {"start": v(-10.74, 29.37) * mm, "end": v(-10.74, 20.63) * mm});
            skLineSegment(sketch, "E73.1.0.2", {"start": v(-24.74, 20.63) * mm, "end": v(-24.74, 29.37) * mm});
            skLineSegment(sketch, "E73.direction1", {"start": v(-67.74, 25) * mm, "end": v(-17.74, 25) * mm, "construction": true});
            skLineSegment(sketch, "E74.1.0.0", {"start": v(25.26, 20.63) * mm, "end": v(25.26, 29.37) * mm});
            skCircle(sketch, "E74.1.0.1", {"center": v(32.26, 25) * mm, "radius": 8.25 * mm});
            skLineSegment(sketch, "E74.1.0.2", {"start": v(39.26, 29.37) * mm, "end": v(39.26, 20.63) * mm});
            skLineSegment(sketch, "E74.direction1", {"start": v(-24.74, 20.63) * mm, "end": v(25.26, 20.63) * mm, "construction": true});
            skCircle(sketch, "E75.1.0.0", {"center": v(72.26, 25) * mm, "radius": 8.25 * mm});
            skLineSegment(sketch, "E75.1.0.1", {"start": v(79.26, 29.37) * mm, "end": v(79.26, 20.63) * mm});
            skLineSegment(sketch, "E75.1.0.2", {"start": v(65.26, 20.63) * mm, "end": v(65.26, 29.37) * mm});
            skLineSegment(sketch, "E75.direction1", {"start": v(32.26, 25) * mm, "end": v(72.26, 25) * mm, "construction": true});
            skCircle(sketch, "E76.0.1.0", {"center": v(-67.74, 50) * mm, "radius": 8.25 * mm});
            skLineSegment(sketch, "E76.0.1.1", {"start": v(-74.74, 45.63) * mm, "end": v(-74.74, 54.37) * mm});
            skLineSegment(sketch, "E76.0.1.2", {"start": v(-60.74, 54.37) * mm, "end": v(-60.74, 45.63) * mm});
            skLineSegment(sketch, "E76.direction1", {"start": v(-67.74, 25) * mm, "end": v(-32.74, 25) * mm, "construction": true});
            skLineSegment(sketch, "E76.direction2", {"start": v(-67.74, 25) * mm, "end": v(-67.74, 50) * mm, "construction": true});
            skCircle(sketch, "E77.0.1.0", {"center": v(-17.74, 50) * mm, "radius": 8.25 * mm});
            skLineSegment(sketch, "E77.0.1.1", {"start": v(-24.74, 45.63) * mm, "end": v(-24.74, 54.37) * mm});
            skLineSegment(sketch, "E77.0.1.2", {"start": v(-10.74, 54.37) * mm, "end": v(-10.74, 45.63) * mm});
            skLineSegment(sketch, "E77.direction1", {"start": v(-17.74, 25) * mm, "end": v(7.26, 25) * mm, "construction": true});
            skLineSegment(sketch, "E77.direction2", {"start": v(-17.74, 25) * mm, "end": v(-17.74, 50) * mm, "construction": true});
            skSolve(sketch);
        }
        {
            var Q0;
            {var subQ0=sQuery(id+"F12.wireOp",EDGE,"E76.0.1.1");Q0=makeQuery(id+"F12.imprint","IMPRINT",FACE,{"disambiguationData":[TD([[makeQuery(id+"F12.imprint","IMPRINT",EDGE,{"derivedFrom":subQ0}),-1.0]])]});}
            var Q1;
            {var subQ0=sQuery(id+"F12.wireOp",EDGE,"E71");Q1=makeQuery(id+"F12.imprint","IMPRINT",FACE,{"disambiguationData":[TD([[makeQuery(id+"F12.imprint","IMPRINT",EDGE,{"derivedFrom":subQ0}),-1.0]])]});}
            var Q2;
            {var subQ0=sQuery(id+"F12.wireOp",EDGE,"E77.0.1.1");Q2=makeQuery(id+"F12.imprint","IMPRINT",FACE,{"disambiguationData":[TD([[makeQuery(id+"F12.imprint","IMPRINT",EDGE,{"derivedFrom":subQ0}),-1.0]])]});}
            var Q3;
            {var subQ0=sQuery(id+"F12.wireOp",EDGE,"E73.1.0.1");Q3=makeQuery(id+"F12.imprint","IMPRINT",FACE,{"disambiguationData":[TD([[makeQuery(id+"F12.imprint","IMPRINT",EDGE,{"derivedFrom":subQ0}),-1.0]])]});}
            extrude(context, id + "F13", {"entities" : qUnion([Q0, Q1, Q2, Q3]), "operationType" : NewBodyOperationType.REMOVE, "endBound" : BoundingType.UP_TO_NEXT, "oppositeDirection" : true, "depth" : 25 * mm});
        }
        {
            var Q0;
            {var subQ1=sQuery(id+"F0.wireOp",EDGE,"E9.1.0.0");var subQ2=sQuery(id+"F0.wireOp",EDGE,"E9.1.1.0");var subQ5=sQuery(id+"F0.wireOp",EDGE,"E15");var subQ7=sQuery(id+"F0.wireOp",EDGE,"E16.MirrorCS");var subQ8=sQuery(id+"F0.wireOp",EDGE,"E14");var subQ10=sQuery(id+"F0.wireOp",EDGE,"E17.MirrorCS");var subQ13=makeQuery(id+"F1.opExtrude","SWEPT_FACE",FACE,{"disambiguationData":[OSD([subQ8])]});var subQ18=sQuery(id+"F0.wireOp",EDGE,"E3.bottom");var subQ19=sQuery(id+"F0.wireOp",EDGE,"E3.top");var subQ20=sQuery(id+"F0.wireOp",EDGE,"E3.left");var subQ21=sQuery(id+"F0.wireOp",EDGE,"E3.right");Q0=makeQuery(id+"F6.boolean.opBoolean","SPLIT",FACE,{"disambiguationData":[TD([subQ13])],"derivedFrom":makeQuery(id+"F2.boolean.opBoolean","SPLIT",FACE,{"disambiguationData":[TD([makeQuery(id+"F1.opExtrude","SWEPT_FACE",FACE,{"disambiguationData":[OSD([subQ18])]})])],"derivedFrom":makeQuery(id+"F1.opExtrude","CAP_FACE",FACE,{"disambiguationData":[OSD([subQ18,subQ19,subQ20,subQ21,subQ1,subQ2,subQ8,subQ5,subQ7,subQ10])],"isStart":true})})});}
            var sketch = newSketch(context, id + "F14", { "sketchPlane" : qUnion([Q0])});
            skLineSegment(sketch, "E78.bottom", {"start": v(-25.27, 28.5) * mm, "end": v(-25.27, 28.5) * mm});
            skLineSegment(sketch, "E78.top", {"start": v(55.73, -28.5) * mm, "end": v(55.73, -28.5) * mm});
            skLineSegment(sketch, "E78.left", {"start": v(-70.27, 28.5) * mm, "end": v(-70.27, -28.5) * mm});
            skLineSegment(sketch, "E78.right", {"start": v(84.73, 28.5) * mm, "end": v(84.73, -28.5) * mm});
            skLineSegment(sketch, "E79.bottom", {"start": v(-70.27, 28.5) * mm, "end": v(-30.27, 28.5) * mm, "construction": true});
            skLineSegment(sketch, "E79.top", {"start": v(-65.27, 43.5) * mm, "end": v(-35.27, 43.5) * mm});
            skLineSegment(sketch, "E79.left", {"start": v(-70.27, 28.5) * mm, "end": v(-70.27, 38.5) * mm});
            skLineSegment(sketch, "E79.right", {"start": v(-30.27, 33.5) * mm, "end": v(-30.27, 38.5) * mm});
            skLineSegment(sketch, "E80.bottom", {"start": v(-20.27, 28.5) * mm, "end": v(50.73, 28.5) * mm, "construction": true});
            skLineSegment(sketch, "E80.top", {"start": v(-15.27, 43.5) * mm, "end": v(45.73, 43.5) * mm});
            skLineSegment(sketch, "E80.left", {"start": v(-20.27, 33.5) * mm, "end": v(-20.27, 38.5) * mm});
            skLineSegment(sketch, "E80.right", {"start": v(50.73, 33.5) * mm, "end": v(50.73, 38.5) * mm});
            skLineSegment(sketch, "E81.bottom", {"start": v(65.73, 43.5) * mm, "end": v(79.73, 43.5) * mm});
            skLineSegment(sketch, "E81.top", {"start": v(60.73, 28.5) * mm, "end": v(84.73, 28.5) * mm, "construction": true});
            skLineSegment(sketch, "E81.left", {"start": v(60.73, 38.5) * mm, "end": v(60.73, 33.5) * mm});
            skLineSegment(sketch, "E81.right", {"start": v(84.73, 38.5) * mm, "end": v(84.73, 28.5) * mm});
            skLineSegment(sketch, "E82.bottom", {"start": v(-70.27, -28.5) * mm, "end": v(-35.27, -28.5) * mm, "construction": true});
            skLineSegment(sketch, "E82.top", {"start": v(-65.27, -43.5) * mm, "end": v(-35.27, -43.5) * mm});
            skLineSegment(sketch, "E82.left", {"start": v(-70.27, -28.5) * mm, "end": v(-70.27, -38.5) * mm});
            skLineSegment(sketch, "E82.right", {"start": v(-30.27, -33.5) * mm, "end": v(-30.27, -38.5) * mm});
            skLineSegment(sketch, "E83.bottom", {"start": v(-20.27, -28.5) * mm, "end": v(50.73, -28.5) * mm, "construction": true});
            skLineSegment(sketch, "E83.top", {"start": v(-15.27, -43.5) * mm, "end": v(45.73, -43.5) * mm});
            skLineSegment(sketch, "E83.left", {"start": v(-20.27, -33.5) * mm, "end": v(-20.27, -38.5) * mm});
            skLineSegment(sketch, "E83.right", {"start": v(50.73, -33.5) * mm, "end": v(50.73, -38.5) * mm});
            skLineSegment(sketch, "E84.bottom", {"start": v(65.73, -43.5) * mm, "end": v(79.73, -43.5) * mm});
            skLineSegment(sketch, "E84.top", {"start": v(60.73, -28.5) * mm, "end": v(84.73, -28.5) * mm, "construction": true});
            skLineSegment(sketch, "E84.left", {"start": v(60.73, -38.5) * mm, "end": v(60.73, -33.5) * mm});
            skLineSegment(sketch, "E84.right", {"start": v(84.73, -38.5) * mm, "end": v(84.73, -28.5) * mm});
            skPoint(sketch, "E85", {"position": v(-25.27, 33) * mm});
            skPoint(sketch, "E86", {"position": v(55.73, 33) * mm});
            skPoint(sketch, "E87.visualSharp", {"position": v(-70.27, 43.5) * mm});
            skArc(sketch, "E87.filletArc", {"start": v(-65.27, 43.5) * mm, "mid": v(-68.8, 42.04) * mm, "end": v(-70.27, 38.5) * mm});
            skPoint(sketch, "E88.visualSharp", {"position": v(-30.27, 43.5) * mm});
            skArc(sketch, "E88.filletArc", {"start": v(-30.27, 38.5) * mm, "mid": v(-31.73, 42.04) * mm, "end": v(-35.27, 43.5) * mm});
            skArc(sketch, "E89.filletArc", {"start": v(-30.27, 33.5) * mm, "mid": v(-28.8, 29.96) * mm, "end": v(-25.27, 28.5) * mm});
            skPoint(sketch, "E90.visualSharp", {"position": v(-20.27, 43.5) * mm});
            skArc(sketch, "E90.filletArc", {"start": v(-15.27, 43.5) * mm, "mid": v(-18.8, 42.04) * mm, "end": v(-20.27, 38.5) * mm});
            skArc(sketch, "E91.filletArc", {"start": v(-25.27, 28.5) * mm, "mid": v(-21.73, 29.96) * mm, "end": v(-20.27, 33.5) * mm});
            skPoint(sketch, "E92.visualSharp", {"position": v(50.73, 43.5) * mm});
            skArc(sketch, "E92.filletArc", {"start": v(50.73, 38.5) * mm, "mid": v(49.27, 42.04) * mm, "end": v(45.73, 43.5) * mm});
            skPoint(sketch, "E93.visualSharp", {"position": v(60.73, 43.5) * mm});
            skArc(sketch, "E93.filletArc", {"start": v(65.73, 43.5) * mm, "mid": v(62.2, 42.04) * mm, "end": v(60.73, 38.5) * mm});
            skPoint(sketch, "E94.visualSharp", {"position": v(84.73, 43.5) * mm});
            skArc(sketch, "E94.filletArc", {"start": v(84.73, 38.5) * mm, "mid": v(83.27, 42.04) * mm, "end": v(79.73, 43.5) * mm});
            skArc(sketch, "E95.filletArc", {"start": v(60.73, -33.5) * mm, "mid": v(59.27, -29.96) * mm, "end": v(55.73, -28.5) * mm});
            skPoint(sketch, "E96.newPointA", {"position": v(50.73, -28.5) * mm});
            skArc(sketch, "E96.filletArc", {"start": v(55.73, -28.5) * mm, "mid": v(52.2, -29.96) * mm, "end": v(50.73, -33.5) * mm});
            skPoint(sketch, "E97.visualSharp", {"position": v(60.73, -43.5) * mm});
            skArc(sketch, "E97.filletArc", {"start": v(60.73, -38.5) * mm, "mid": v(62.2, -42.04) * mm, "end": v(65.73, -43.5) * mm});
            skPoint(sketch, "E98.visualSharp", {"position": v(84.73, -43.5) * mm});
            skArc(sketch, "E98.filletArc", {"start": v(79.73, -43.5) * mm, "mid": v(83.27, -42.04) * mm, "end": v(84.73, -38.5) * mm});
            skPoint(sketch, "E99.visualSharp", {"position": v(50.73, -43.5) * mm});
            skArc(sketch, "E99.filletArc", {"start": v(45.73, -43.5) * mm, "mid": v(49.27, -42.04) * mm, "end": v(50.73, -38.5) * mm});
            skPoint(sketch, "E100.visualSharp", {"position": v(-20.27, -43.5) * mm});
            skArc(sketch, "E100.filletArc", {"start": v(-20.27, -38.5) * mm, "mid": v(-18.8, -42.04) * mm, "end": v(-15.27, -43.5) * mm});
            skPoint(sketch, "E101.visualSharp", {"position": v(-30.27, -43.5) * mm});
            skArc(sketch, "E101.filletArc", {"start": v(-35.27, -43.5) * mm, "mid": v(-31.73, -42.04) * mm, "end": v(-30.27, -38.5) * mm});
            skPoint(sketch, "E102.visualSharp", {"position": v(-70.27, -43.5) * mm});
            skArc(sketch, "E102.filletArc", {"start": v(-70.27, -38.5) * mm, "mid": v(-68.8, -42.04) * mm, "end": v(-65.27, -43.5) * mm});
            skPoint(sketch, "E103.visualSharp", {"position": v(-30.27, -28.5) * mm});
            skLineSegment(sketch, "E104", {"start": v(-25.27, -28.5) * mm, "end": v(-25.27, -28.5) * mm});
            skLineSegment(sketch, "E105", {"start": v(-30.27, -33.5) * mm, "end": v(-30.27, -33.5) * mm});
            skLineSegment(sketch, "E106", {"start": v(55.73, 28.5) * mm, "end": v(55.73, 28.5) * mm});
            skPoint(sketch, "E107.visualSharp", {"position": v(50.73, 28.5) * mm});
            skArc(sketch, "E107.filletArc", {"start": v(50.73, 33.5) * mm, "mid": v(52.2, 29.96) * mm, "end": v(55.73, 28.5) * mm});
            skArc(sketch, "E108.filletArc", {"start": v(-25.27, -28.5) * mm, "mid": v(-28.8, -29.96) * mm, "end": v(-30.27, -33.5) * mm});
            skPoint(sketch, "E109.visualSharp", {"position": v(60.73, 28.5) * mm});
            skArc(sketch, "E109.filletArc", {"start": v(55.73, 28.5) * mm, "mid": v(59.27, 29.96) * mm, "end": v(60.73, 33.5) * mm});
            skPoint(sketch, "E110.visualSharp", {"position": v(-20.27, -28.5) * mm});
            skArc(sketch, "E110.filletArc", {"start": v(-20.27, -33.5) * mm, "mid": v(-21.73, -29.96) * mm, "end": v(-25.27, -28.5) * mm});
            skSolve(sketch);
        }
        {
            var Q0;
            Q0=makeQuery(id+"F14.imprint","IMPRINT",FACE,{"disambiguationData":[TD([[makeQuery(id+"F14.imprint","IMPRINT",EDGE,{"derivedFrom":sQuery(id+"F14.wireOp",EDGE,"E78.left")}),1.0]])]});
            var Q1;
            Q1=makeQuery(id+"F14.imprint","IMPRINT",FACE,{"disambiguationData":[TD([[makeQuery(id+"F14.imprint","IMPRINT",EDGE,{"derivedFrom":sQuery(id+"F14.wireOp",EDGE,"E78.left")}),1.0]])]});
            extrude(context, id + "F15", {"entities" : qUnion([Q0, Q1]), "operationType" : NewBodyOperationType.REMOVE, "oppositeDirection" : true, "depth" : 2 * mm});
        }
    });
